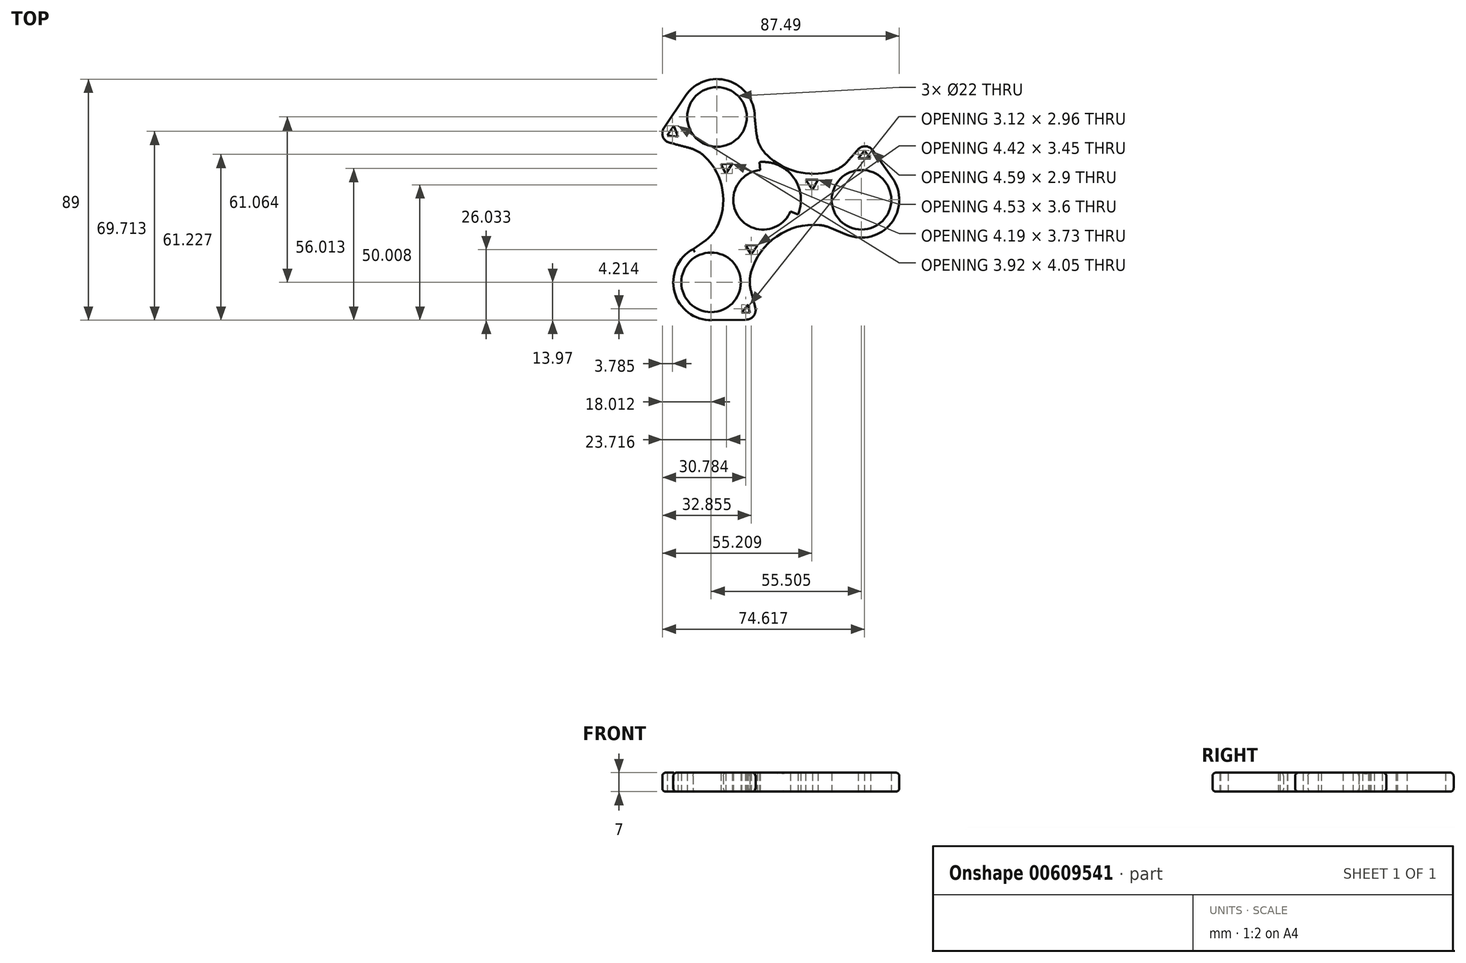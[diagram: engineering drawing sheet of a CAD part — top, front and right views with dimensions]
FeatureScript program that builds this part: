
annotation { "Feature Type Name" : "Feature", "Feature Type Description" : "" }
export const myFeature = defineFeature(function(context is Context, id is Id, definition is map)
    precondition{}
    {
        {
            var Q0;
            Q0=qCreatedBy(makeId("Top.planeOp"),FACE);
            var sketch = newSketch(context, id + "F0", { "sketchPlane" : qUnion([Q0])});
            skLineSegment(sketch, "E0.0", {"start": v(-17.02, 30.58) * mm, "end": v(17.02, 30.58) * mm});
            skLineSegment(sketch, "E0.4", {"start": v(-19.19, -30.48) * mm, "end": v(-35.75, 0) * mm});
            skLineSegment(sketch, "E0.5", {"start": v(-35.75, 0) * mm, "end": v(-17.02, 30.58) * mm});
            skPoint(sketch, "E0.0.midPoint", {"position": v(0, 30.58) * mm});
            skCircle(sketch, "E1", {"center": v(-19.19, -30.48) * mm, "radius": 13.97 * mm});
            skCircle(sketch, "E2", {"center": v(36.32, 0) * mm, "radius": 13.97 * mm});
            skCircle(sketch, "E3", {"center": v(-17.02, 30.58) * mm, "radius": 13.97 * mm});
            skLineSegment(sketch, "E4", {"start": v(-25.86, -18.2) * mm, "end": v(0, 0) * mm});
            skLineSegment(sketch, "E5", {"start": v(0, 0) * mm, "end": v(33.25, -13.86) * mm});
            skLineSegment(sketch, "E6", {"start": v(-3.05, 30.58) * mm, "end": v(0, 0) * mm});
            skPoint(sketch, "E7.0.internal.snap0", {"position": v(0, -30.48) * mm});
            skPoint(sketch, "E8.2.internal.snap0", {"position": v(-9.15, 6.18) * mm});
            skPoint(sketch, "E9.2.internal.snap0", {"position": v(1.12, 10.36) * mm});
            skPoint(sketch, "E10.0.midPoint", {"position": v(0, 45.22) * mm});
            skFitSpline(sketch, "E11", {"points": [v(-5.22, -30.86) * mm, v(-1.7, -44.15) * mm], "startDerivative": vector(4.04, -14.04) * mm, "endDerivative": vector(4.04, -14.04) * mm});
            skFitSpline(sketch, "E12", {"points": [v(38.06, 21.73) * mm, v(28.86, 11.82) * mm], "startDerivative": vector(-10.65, -10) * mm, "endDerivative": vector(-10.65, -10) * mm});
            skFitSpline(sketch, "E13", {"points": [v(-39.36, 22.35) * mm, v(-24.69, 18.5) * mm], "startDerivative": vector(14.18, -3.53) * mm, "endDerivative": vector(14.18, -3.53) * mm});
            skLineSegment(sketch, "E14", {"start": v(-28.63, 38.36) * mm, "end": v(-39.36, 22.35) * mm});
            skLineSegment(sketch, "E15", {"start": v(38.06, 21.73) * mm, "end": v(47.72, 8.07) * mm});
            skLineSegment(sketch, "E16", {"start": v(-18.95, -44.45) * mm, "end": v(-1.7, -44.15) * mm});
            skCircle(sketch, "E17", {"center": v(-17.02, 30.58) * mm, "radius": 11 * mm});
            skCircle(sketch, "E18", {"center": v(36.32, 0) * mm, "radius": 11 * mm});
            skCircle(sketch, "E19", {"center": v(-19.19, -30.48) * mm, "radius": 11 * mm});
            skCircle(sketch, "E20", {"center": v(0, 0) * mm, "radius": 13.97 * mm});
            skCircle(sketch, "E21", {"center": v(0, 0) * mm, "radius": 11 * mm});
            skArc(sketch, "E22", {"start": v(23.12, -9.63) * mm, "mid": v(4.3, -14.03) * mm, "end": v(-5.22, -30.86) * mm});
            skArc(sketch, "E23", {"start": v(-2.06, 20.65) * mm, "mid": v(11.78, 10.56) * mm, "end": v(28.86, 11.82) * mm});
            skArc(sketch, "E24", {"start": v(-19.19, -13.5) * mm, "mid": v(-15, 3.68) * mm, "end": v(-24.69, 18.5) * mm});
            skLineSegment(sketch, "E25", {"start": v(23.12, -9.63) * mm, "end": v(33.25, -13.86) * mm});
            skLineSegment(sketch, "E26", {"start": v(10.45, -4.35) * mm, "end": v(33.25, -13.86) * mm});
            skLineSegment(sketch, "E27", {"start": v(-35.37, 23.76) * mm, "end": v(-33, 27.29) * mm});
            skLineSegment(sketch, "E28", {"start": v(-33, 27.29) * mm, "end": v(-31.46, 23.24) * mm});
            skLineSegment(sketch, "E29", {"start": v(-31.46, 23.24) * mm, "end": v(-35.37, 23.76) * mm});
            skPoint(sketch, "E30.endSnap0", {"position": v(42.9, 14.9) * mm});
            skLineSegment(sketch, "E31", {"start": v(-15.58, 13.08) * mm, "end": v(-13.74, 9.7) * mm});
            skLineSegment(sketch, "E32", {"start": v(-13.74, 9.7) * mm, "end": v(-11.4, 13.43) * mm});
            skLineSegment(sketch, "E33", {"start": v(-11.4, 13.43) * mm, "end": v(-15.58, 13.08) * mm});
            skLineSegment(sketch, "E34", {"start": v(-4.34, -20.14) * mm, "end": v(-2.13, -16.83) * mm});
            skLineSegment(sketch, "E35", {"start": v(-2.13, -16.83) * mm, "end": v(-6.56, -16.69) * mm});
            skLineSegment(sketch, "E36", {"start": v(-6.56, -16.69) * mm, "end": v(-4.34, -20.14) * mm});
            skLineSegment(sketch, "E37", {"start": v(15.74, 7.36) * mm, "end": v(20.27, 7.36) * mm});
            skLineSegment(sketch, "E38", {"start": v(20.27, 7.36) * mm, "end": v(18.17, 3.76) * mm});
            skLineSegment(sketch, "E39", {"start": v(18.17, 3.76) * mm, "end": v(15.74, 7.36) * mm});
            skLineSegment(sketch, "E40", {"start": v(35.12, 15.33) * mm, "end": v(39.71, 15.33) * mm});
            skLineSegment(sketch, "E41", {"start": v(39.71, 15.33) * mm, "end": v(37.39, 18.23) * mm});
            skLineSegment(sketch, "E42", {"start": v(37.39, 18.23) * mm, "end": v(35.12, 15.33) * mm});
            skLineSegment(sketch, "E43", {"start": v(-7.98, -41.63) * mm, "end": v(-5.51, -38.76) * mm});
            skLineSegment(sketch, "E44", {"start": v(-5.51, -38.76) * mm, "end": v(-4.85, -41.71) * mm});
            skLineSegment(sketch, "E45", {"start": v(-4.85, -41.71) * mm, "end": v(-7.98, -41.63) * mm});
            skSolve(sketch);
        }
        {
            var Q0;
            {var subQ0=sQuery(id+"F0.wireOp",EDGE,"E3");var subQ2=sQuery(id+"F0.wireOp",EDGE,"E0.5");var subQ3=makeQuery(id+"F0.imprint","INTERSECT",VERTEX,{"derivedFrom":[subQ2,subQ0]});Q0=makeQuery(id+"F0.imprint","IMPRINT",FACE,{"disambiguationData":[TD([[makeQuery(id+"F0.imprint","IMPRINT",EDGE,{"disambiguationData":[TD([[subQ3,-1.0]])],"derivedFrom":subQ2}),1.0]])]});}
            var Q1;
            {var subQ0=sQuery(id+"F0.wireOp",EDGE,"E13");Q1=makeQuery(id+"F0.imprint","IMPRINT",FACE,{"disambiguationData":[TD([[makeQuery(id+"F0.imprint","IMPRINT",EDGE,{"derivedFrom":subQ0}),1.0]])]});}
            var Q2;
            {var subQ0=sQuery(id+"F0.wireOp",EDGE,"E3");var subQ5=sQuery(id+"F0.wireOp",EDGE,"E0.5");var subQ6=makeQuery(id+"F0.imprint","INTERSECT",VERTEX,{"derivedFrom":[subQ5,subQ0]});Q2=makeQuery(id+"F0.imprint","IMPRINT",FACE,{"disambiguationData":[TD([[makeQuery(id+"F0.imprint","IMPRINT",EDGE,{"disambiguationData":[TD([[subQ6,-1.0]])],"derivedFrom":subQ5}),-1.0]])]});}
            var Q3;
            Q3=makeQuery(id+"F0.imprint","IMPRINT",FACE,{"disambiguationData":[TD([[makeQuery(id+"F0.imprint","IMPRINT",EDGE,{"derivedFrom":sQuery(id+"F0.wireOp",EDGE,"E31")}),-1.0]])]});
            var Q4;
            {var subQ0=sQuery(id+"F0.wireOp",EDGE,"E20");var subQ1=sQuery(id+"F0.wireOp",EDGE,"E4");var subQ2=makeQuery(id+"F0.imprint","INTERSECT",VERTEX,{"derivedFrom":[subQ1,subQ0]});Q4=makeQuery(id+"F0.imprint","IMPRINT",FACE,{"disambiguationData":[TD([[makeQuery(id+"F0.imprint","IMPRINT",EDGE,{"disambiguationData":[TD([[subQ2,-1.0]])],"derivedFrom":subQ1}),1.0]])]});}
            var Q5;
            {var subQ1=sQuery(id+"F0.wireOp",EDGE,"E5");var subQ7=sQuery(id+"F0.wireOp",EDGE,"E26");var subQ9=makeQuery(id+"F0.imprint","INTERSECT",VERTEX,{"derivedFrom":[subQ1,subQ7]});Q5=makeQuery(id+"F0.imprint","IMPRINT",FACE,{"disambiguationData":[TD([[makeQuery(id+"F0.imprint","IMPRINT",EDGE,{"disambiguationData":[TD([[subQ9,1.0]])],"derivedFrom":subQ1}),1.0]])]});}
            var Q6;
            {var subQ0=sQuery(id+"F0.wireOp",EDGE,"E23");Q6=makeQuery(id+"F0.imprint","IMPRINT",FACE,{"disambiguationData":[TD([[makeQuery(id+"F0.imprint","IMPRINT",EDGE,{"derivedFrom":subQ0}),-1.0]])]});}
            var Q7;
            Q7=makeQuery(id+"F0.imprint","IMPRINT",FACE,{"disambiguationData":[TD([[makeQuery(id+"F0.imprint","IMPRINT",EDGE,{"derivedFrom":sQuery(id+"F0.wireOp",EDGE,"E18")}),-1.0]])]});
            var Q8;
            {var subQ8=sQuery(id+"F0.wireOp",EDGE,"E22");Q8=makeQuery(id+"F0.imprint","IMPRINT",FACE,{"disambiguationData":[TD([[makeQuery(id+"F0.imprint","IMPRINT",EDGE,{"derivedFrom":subQ8}),-1.0]])]});}
            var Q9;
            {var subQ1=sQuery(id+"F0.wireOp",EDGE,"E4");var subQ7=sQuery(id+"F0.wireOp",EDGE,"E20");var subQ8=makeQuery(id+"F0.imprint","INTERSECT",VERTEX,{"derivedFrom":[subQ1,subQ7]});Q9=makeQuery(id+"F0.imprint","IMPRINT",FACE,{"disambiguationData":[TD([[makeQuery(id+"F0.imprint","IMPRINT",EDGE,{"disambiguationData":[TD([[subQ8,-1.0]])],"derivedFrom":subQ1}),-1.0]])]});}
            var Q10;
            {var subQ1=sQuery(id+"F0.wireOp",EDGE,"E0.3");var subQ3=sQuery(id+"F0.wireOp",EDGE,"E19");var subQ4=makeQuery(id+"F0.imprint","INTERSECT",VERTEX,{"derivedFrom":[subQ1,subQ3]});Q10=makeQuery(id+"F0.imprint","IMPRINT",FACE,{"disambiguationData":[TD([[makeQuery(id+"F0.imprint","IMPRINT",EDGE,{"disambiguationData":[TD([[subQ4,-1.0]])],"derivedFrom":subQ3}),-1.0]])]});}
            var Q11;
            {var subQ1=sQuery(id+"F0.wireOp",EDGE,"E11");Q11=makeQuery(id+"F0.imprint","IMPRINT",FACE,{"disambiguationData":[TD([[makeQuery(id+"F0.imprint","IMPRINT",EDGE,{"derivedFrom":subQ1}),-1.0]])]});}
            var Q12;
            {var subQ3=sQuery(id+"F0.wireOp",EDGE,"E12");Q12=makeQuery(id+"F0.imprint","IMPRINT",FACE,{"disambiguationData":[TD([[makeQuery(id+"F0.imprint","IMPRINT",EDGE,{"derivedFrom":subQ3}),1.0]])]});}
            var Q13;
            {var subQ1=sQuery(id+"F0.wireOp",EDGE,"E0.3");var subQ4=sQuery(id+"F0.wireOp",EDGE,"E19");var subQ5=makeQuery(id+"F0.imprint","INTERSECT",VERTEX,{"derivedFrom":[subQ1,subQ4]});Q13=makeQuery(id+"F0.imprint","IMPRINT",FACE,{"disambiguationData":[TD([[makeQuery(id+"F0.imprint","IMPRINT",EDGE,{"disambiguationData":[TD([[subQ5,1.0]])],"derivedFrom":subQ4}),-1.0]])]});}
            var Q14;
            Q14=makeQuery(id+"F0.imprint","IMPRINT",FACE,{"disambiguationData":[TD([[makeQuery(id+"F0.imprint","IMPRINT",EDGE,{"derivedFrom":sQuery(id+"F0.wireOp",EDGE,"E19")}),-1.0]])]});
            extrude(context, id + "F1", {"entities" : qUnion([Q0, Q1, Q2, Q3, Q4, Q5, Q6, Q7, Q8, Q9, Q10, Q11, Q12, Q13, Q14]), "depth" : 7 * mm, "offsetDistance" : 25.4 * mm});
        }
        {
            var Q0;
            Q0=makeQuery(id+"F1.opExtrude","SWEPT_EDGE",EDGE,{"disambiguationData":[OSD([sQuery(id+"F0.wireOp",EDGE,"E13"),sQuery(id+"F0.wireOp",EDGE,"E24")])]});
            fillet(context, id + "F2", {"entities" : qUnion([Q0]), "radius" : 12.7 * mm, "tangentPropagation" : true, "rho" : 0.5, "crossSection" : FilletCrossSection.CONIC, "allowEdgeOverflow" : false});
        }
        {
            var Q0;
            Q0=makeQuery(id+"F1.opExtrude","SWEPT_EDGE",EDGE,{"disambiguationData":[OSD([sQuery(id+"F0.wireOp",EDGE,"E0.3"),sQuery(id+"F0.wireOp",EDGE,"E1"),sQuery(id+"F0.wireOp",EDGE,"E11"),sQuery(id+"F0.wireOp",EDGE,"E22")])]});
            var Q1;
            Q1=makeQuery(id+"F1.opExtrude","SWEPT_EDGE",EDGE,{"disambiguationData":[OSD([sQuery(id+"F0.wireOp",EDGE,"E0.1"),sQuery(id+"F0.wireOp",EDGE,"E2"),sQuery(id+"F0.wireOp",EDGE,"E12"),sQuery(id+"F0.wireOp",EDGE,"E23")])]});
            fillet(context, id + "F3", {"entities" : qUnion([Q0, Q1]), "radius" : 12.7 * mm, "tangentPropagation" : true, "rho" : 0.5, "crossSection" : FilletCrossSection.CONIC, "allowEdgeOverflow" : false});
        }
        {
            var Q0;
            Q0=makeQuery(id+"F1.opExtrude","SWEPT_EDGE",EDGE,{"disambiguationData":[OSD([sQuery(id+"F0.wireOp",EDGE,"E6"),sQuery(id+"F0.wireOp",EDGE,"E23")])]});
            var Q1;
            Q1=makeQuery(id+"F1.opExtrude","SWEPT_EDGE",EDGE,{"disambiguationData":[OSD([sQuery(id+"F0.wireOp",EDGE,"E4"),sQuery(id+"F0.wireOp",EDGE,"E24")])]});
            var Q2;
            Q2=makeQuery(id+"F1.opExtrude","SWEPT_EDGE",EDGE,{"disambiguationData":[OSD([sQuery(id+"F0.wireOp",EDGE,"E22"),sQuery(id+"F0.wireOp",EDGE,"E26")])]});
            fillet(context, id + "F4", {"entities" : qUnion([Q0, Q1, Q2]), "radius" : 12.7 * mm, "tangentPropagation" : true, "allowEdgeOverflow" : false});
        }
        {
            var Q0;
            Q0=makeQuery(id+"F1.opExtrude","CAP_EDGE",EDGE,{"disambiguationData":[OSD([sQuery(id+"F0.wireOp",EDGE,"E24")])],"isStart":false});
            var Q1;
            {var subQ0=sQuery(id+"F0.wireOp",EDGE,"E24");var subQ1=sQuery(id+"F0.wireOp",EDGE,"E13");Q1=makeQuery(id+"F2.opFillet","BLEND_EDGE",EDGE,{"blendedFrom":[makeQuery(id+"F1.opExtrude","SWEPT_EDGE",EDGE,{"disambiguationData":[OSD([subQ1,subQ0])]}),makeQuery(id+"F1.opExtrude","CAP_FACE",FACE,{"disambiguationData":[OSD([sQuery(id+"F0.wireOp",EDGE,"E1"),sQuery(id+"F0.wireOp",EDGE,"E2"),sQuery(id+"F0.wireOp",EDGE,"E3"),sQuery(id+"F0.wireOp",EDGE,"E4"),sQuery(id+"F0.wireOp",EDGE,"E6"),sQuery(id+"F0.wireOp",EDGE,"E11"),sQuery(id+"F0.wireOp",EDGE,"E12"),subQ1,sQuery(id+"F0.wireOp",EDGE,"E14"),sQuery(id+"F0.wireOp",EDGE,"E15"),sQuery(id+"F0.wireOp",EDGE,"E16"),sQuery(id+"F0.wireOp",EDGE,"E17"),sQuery(id+"F0.wireOp",EDGE,"E18"),sQuery(id+"F0.wireOp",EDGE,"E19"),sQuery(id+"F0.wireOp",EDGE,"E21"),sQuery(id+"F0.wireOp",EDGE,"E22"),sQuery(id+"F0.wireOp",EDGE,"E23"),subQ0,sQuery(id+"F0.wireOp",EDGE,"E26"),sQuery(id+"F0.wireOp",EDGE,"E27"),sQuery(id+"F0.wireOp",EDGE,"E28"),sQuery(id+"F0.wireOp",EDGE,"E29"),sQuery(id+"F0.wireOp",EDGE,"GTHNUjAg-pZz5-5pDl-8vrh-2y5vtAJtB5Yq"),sQuery(id+"F0.wireOp",EDGE,"E30"),sQuery(id+"F0.wireOp",EDGE,"ZPwYMNyf-sNfp-RKr8-1Stz-misUmBmXIjCw"),sQuery(id+"F0.wireOp",EDGE,"XcAcG1Qn-K1HW-D48b-8TJg-uuhdHlqaHKt2"),sQuery(id+"F0.wireOp",EDGE,"NuKtL48T-xxGD-nBnq-HVJp-iiLt3Cd7KKB5"),sQuery(id+"F0.wireOp",EDGE,"xELJaT0b-NjaD-HxtK-KQ1K-Fbe63v3JBSdq"),sQuery(id+"F0.wireOp",EDGE,"E31"),sQuery(id+"F0.wireOp",EDGE,"E32"),sQuery(id+"F0.wireOp",EDGE,"E33"),sQuery(id+"F0.wireOp",EDGE,"SiT3KE0M-eyeN-RMu0-dXW5-lyOyQHbvpu54"),sQuery(id+"F0.wireOp",EDGE,"M9HWfai5-cRg1-bBkV-RGF1-t70geMIoM3zD"),sQuery(id+"F0.wireOp",EDGE,"RyxoEFKP-Jya3-Pohf-oNvh-z6z1ak4gsZTN"),sQuery(id+"F0.wireOp",EDGE,"E34"),sQuery(id+"F0.wireOp",EDGE,"E35"),sQuery(id+"F0.wireOp",EDGE,"E36")])],"isStart":false})],"blendedInto":[makeQuery(id+"F1.opExtrude","CAP_FACE",FACE,{"disambiguationData":[OSD([sQuery(id+"F0.wireOp",EDGE,"E1"),sQuery(id+"F0.wireOp",EDGE,"E2"),sQuery(id+"F0.wireOp",EDGE,"E3"),sQuery(id+"F0.wireOp",EDGE,"E4"),sQuery(id+"F0.wireOp",EDGE,"E6"),sQuery(id+"F0.wireOp",EDGE,"E11"),sQuery(id+"F0.wireOp",EDGE,"E12"),subQ1,sQuery(id+"F0.wireOp",EDGE,"E14"),sQuery(id+"F0.wireOp",EDGE,"E15"),sQuery(id+"F0.wireOp",EDGE,"E16"),sQuery(id+"F0.wireOp",EDGE,"E17"),sQuery(id+"F0.wireOp",EDGE,"E18"),sQuery(id+"F0.wireOp",EDGE,"E19"),sQuery(id+"F0.wireOp",EDGE,"E21"),sQuery(id+"F0.wireOp",EDGE,"E22"),sQuery(id+"F0.wireOp",EDGE,"E23"),subQ0,sQuery(id+"F0.wireOp",EDGE,"E26"),sQuery(id+"F0.wireOp",EDGE,"E27"),sQuery(id+"F0.wireOp",EDGE,"E28"),sQuery(id+"F0.wireOp",EDGE,"E29"),sQuery(id+"F0.wireOp",EDGE,"GTHNUjAg-pZz5-5pDl-8vrh-2y5vtAJtB5Yq"),sQuery(id+"F0.wireOp",EDGE,"E30"),sQuery(id+"F0.wireOp",EDGE,"ZPwYMNyf-sNfp-RKr8-1Stz-misUmBmXIjCw"),sQuery(id+"F0.wireOp",EDGE,"XcAcG1Qn-K1HW-D48b-8TJg-uuhdHlqaHKt2"),sQuery(id+"F0.wireOp",EDGE,"NuKtL48T-xxGD-nBnq-HVJp-iiLt3Cd7KKB5"),sQuery(id+"F0.wireOp",EDGE,"xELJaT0b-NjaD-HxtK-KQ1K-Fbe63v3JBSdq"),sQuery(id+"F0.wireOp",EDGE,"E31"),sQuery(id+"F0.wireOp",EDGE,"E32"),sQuery(id+"F0.wireOp",EDGE,"E33"),sQuery(id+"F0.wireOp",EDGE,"SiT3KE0M-eyeN-RMu0-dXW5-lyOyQHbvpu54"),sQuery(id+"F0.wireOp",EDGE,"M9HWfai5-cRg1-bBkV-RGF1-t70geMIoM3zD"),sQuery(id+"F0.wireOp",EDGE,"RyxoEFKP-Jya3-Pohf-oNvh-z6z1ak4gsZTN"),sQuery(id+"F0.wireOp",EDGE,"E34"),sQuery(id+"F0.wireOp",EDGE,"E35"),sQuery(id+"F0.wireOp",EDGE,"E36")])],"isStart":false})]});}
            var Q2;
            Q2=makeQuery(id+"F1.opExtrude","CAP_EDGE",EDGE,{"disambiguationData":[OSD([sQuery(id+"F0.wireOp",EDGE,"E13")])],"isStart":false});
            var Q3;
            Q3=makeQuery(id+"F1.opExtrude","CAP_EDGE",EDGE,{"disambiguationData":[OSD([sQuery(id+"F0.wireOp",EDGE,"E14")])],"isStart":false});
            var Q4;
            Q4=makeQuery(id+"F1.opExtrude","CAP_EDGE",EDGE,{"disambiguationData":[OSD([sQuery(id+"F0.wireOp",EDGE,"E3")])],"isStart":false});
            var Q5;
            {var subQ0=sQuery(id+"F0.wireOp",EDGE,"E23");var subQ1=sQuery(id+"F0.wireOp",EDGE,"E12");var subQ2=sQuery(id+"F0.wireOp",EDGE,"E2");Q5=makeQuery(id+"F3.opFillet","BLEND_EDGE",EDGE,{"blendedFrom":[makeQuery(id+"F1.opExtrude","SWEPT_EDGE",EDGE,{"disambiguationData":[OSD([sQuery(id+"F0.wireOp",EDGE,"E0.1"),subQ2,subQ1,subQ0])]}),makeQuery(id+"F1.opExtrude","CAP_FACE",FACE,{"disambiguationData":[OSD([sQuery(id+"F0.wireOp",EDGE,"E1"),subQ2,sQuery(id+"F0.wireOp",EDGE,"E3"),sQuery(id+"F0.wireOp",EDGE,"E4"),sQuery(id+"F0.wireOp",EDGE,"E6"),sQuery(id+"F0.wireOp",EDGE,"E11"),subQ1,sQuery(id+"F0.wireOp",EDGE,"E13"),sQuery(id+"F0.wireOp",EDGE,"E14"),sQuery(id+"F0.wireOp",EDGE,"E15"),sQuery(id+"F0.wireOp",EDGE,"E16"),sQuery(id+"F0.wireOp",EDGE,"E17"),sQuery(id+"F0.wireOp",EDGE,"E18"),sQuery(id+"F0.wireOp",EDGE,"E19"),sQuery(id+"F0.wireOp",EDGE,"E21"),sQuery(id+"F0.wireOp",EDGE,"E22"),subQ0,sQuery(id+"F0.wireOp",EDGE,"E24"),sQuery(id+"F0.wireOp",EDGE,"E26"),sQuery(id+"F0.wireOp",EDGE,"E27"),sQuery(id+"F0.wireOp",EDGE,"E28"),sQuery(id+"F0.wireOp",EDGE,"E29"),sQuery(id+"F0.wireOp",EDGE,"GTHNUjAg-pZz5-5pDl-8vrh-2y5vtAJtB5Yq"),sQuery(id+"F0.wireOp",EDGE,"E30"),sQuery(id+"F0.wireOp",EDGE,"ZPwYMNyf-sNfp-RKr8-1Stz-misUmBmXIjCw"),sQuery(id+"F0.wireOp",EDGE,"XcAcG1Qn-K1HW-D48b-8TJg-uuhdHlqaHKt2"),sQuery(id+"F0.wireOp",EDGE,"NuKtL48T-xxGD-nBnq-HVJp-iiLt3Cd7KKB5"),sQuery(id+"F0.wireOp",EDGE,"xELJaT0b-NjaD-HxtK-KQ1K-Fbe63v3JBSdq"),sQuery(id+"F0.wireOp",EDGE,"E31"),sQuery(id+"F0.wireOp",EDGE,"E32"),sQuery(id+"F0.wireOp",EDGE,"E33"),sQuery(id+"F0.wireOp",EDGE,"SiT3KE0M-eyeN-RMu0-dXW5-lyOyQHbvpu54"),sQuery(id+"F0.wireOp",EDGE,"M9HWfai5-cRg1-bBkV-RGF1-t70geMIoM3zD"),sQuery(id+"F0.wireOp",EDGE,"RyxoEFKP-Jya3-Pohf-oNvh-z6z1ak4gsZTN"),sQuery(id+"F0.wireOp",EDGE,"E34"),sQuery(id+"F0.wireOp",EDGE,"E35"),sQuery(id+"F0.wireOp",EDGE,"E36")])],"isStart":false})],"blendedInto":[makeQuery(id+"F1.opExtrude","CAP_FACE",FACE,{"disambiguationData":[OSD([sQuery(id+"F0.wireOp",EDGE,"E1"),subQ2,sQuery(id+"F0.wireOp",EDGE,"E3"),sQuery(id+"F0.wireOp",EDGE,"E4"),sQuery(id+"F0.wireOp",EDGE,"E6"),sQuery(id+"F0.wireOp",EDGE,"E11"),subQ1,sQuery(id+"F0.wireOp",EDGE,"E13"),sQuery(id+"F0.wireOp",EDGE,"E14"),sQuery(id+"F0.wireOp",EDGE,"E15"),sQuery(id+"F0.wireOp",EDGE,"E16"),sQuery(id+"F0.wireOp",EDGE,"E17"),sQuery(id+"F0.wireOp",EDGE,"E18"),sQuery(id+"F0.wireOp",EDGE,"E19"),sQuery(id+"F0.wireOp",EDGE,"E21"),sQuery(id+"F0.wireOp",EDGE,"E22"),subQ0,sQuery(id+"F0.wireOp",EDGE,"E24"),sQuery(id+"F0.wireOp",EDGE,"E26"),sQuery(id+"F0.wireOp",EDGE,"E27"),sQuery(id+"F0.wireOp",EDGE,"E28"),sQuery(id+"F0.wireOp",EDGE,"E29"),sQuery(id+"F0.wireOp",EDGE,"GTHNUjAg-pZz5-5pDl-8vrh-2y5vtAJtB5Yq"),sQuery(id+"F0.wireOp",EDGE,"E30"),sQuery(id+"F0.wireOp",EDGE,"ZPwYMNyf-sNfp-RKr8-1Stz-misUmBmXIjCw"),sQuery(id+"F0.wireOp",EDGE,"XcAcG1Qn-K1HW-D48b-8TJg-uuhdHlqaHKt2"),sQuery(id+"F0.wireOp",EDGE,"NuKtL48T-xxGD-nBnq-HVJp-iiLt3Cd7KKB5"),sQuery(id+"F0.wireOp",EDGE,"xELJaT0b-NjaD-HxtK-KQ1K-Fbe63v3JBSdq"),sQuery(id+"F0.wireOp",EDGE,"E31"),sQuery(id+"F0.wireOp",EDGE,"E32"),sQuery(id+"F0.wireOp",EDGE,"E33"),sQuery(id+"F0.wireOp",EDGE,"SiT3KE0M-eyeN-RMu0-dXW5-lyOyQHbvpu54"),sQuery(id+"F0.wireOp",EDGE,"M9HWfai5-cRg1-bBkV-RGF1-t70geMIoM3zD"),sQuery(id+"F0.wireOp",EDGE,"RyxoEFKP-Jya3-Pohf-oNvh-z6z1ak4gsZTN"),sQuery(id+"F0.wireOp",EDGE,"E34"),sQuery(id+"F0.wireOp",EDGE,"E35"),sQuery(id+"F0.wireOp",EDGE,"E36")])],"isStart":false})]});}
            var Q6;
            Q6=makeQuery(id+"F1.opExtrude","CAP_EDGE",EDGE,{"disambiguationData":[OSD([sQuery(id+"F0.wireOp",EDGE,"E12")])],"isStart":false});
            var Q7;
            Q7=makeQuery(id+"F1.opExtrude","CAP_EDGE",EDGE,{"disambiguationData":[OSD([sQuery(id+"F0.wireOp",EDGE,"E15")])],"isStart":false});
            var Q8;
            Q8=makeQuery(id+"F1.opExtrude","CAP_EDGE",EDGE,{"disambiguationData":[OSD([sQuery(id+"F0.wireOp",EDGE,"E2")])],"isStart":false});
            var Q9;
            Q9=makeQuery(id+"F1.opExtrude","CAP_EDGE",EDGE,{"disambiguationData":[OSD([sQuery(id+"F0.wireOp",EDGE,"E16")])],"isStart":false});
            var Q10;
            Q10=makeQuery(id+"F1.opExtrude","CAP_EDGE",EDGE,{"disambiguationData":[OSD([sQuery(id+"F0.wireOp",EDGE,"E1")])],"isStart":false});
            var Q11;
            Q11=makeQuery(id+"F1.opExtrude","CAP_EDGE",EDGE,{"disambiguationData":[OSD([sQuery(id+"F0.wireOp",EDGE,"E14")])],"isStart":true});
            var Q12;
            Q12=makeQuery(id+"F1.opExtrude","SWEPT_FACE",FACE,{"disambiguationData":[OSD([sQuery(id+"F0.wireOp",EDGE,"E3")])]});
            var Q13;
            {var subQ0=sQuery(id+"F0.wireOp",EDGE,"E23");var subQ1=sQuery(id+"F0.wireOp",EDGE,"E6");Q13=makeQuery(id+"F4.opFillet","BLEND_EDGE",EDGE,{"blendedFrom":[makeQuery(id+"F1.opExtrude","SWEPT_EDGE",EDGE,{"disambiguationData":[OSD([subQ1,subQ0])]}),makeQuery(id+"F1.opExtrude","CAP_FACE",FACE,{"disambiguationData":[OSD([sQuery(id+"F0.wireOp",EDGE,"E1"),sQuery(id+"F0.wireOp",EDGE,"E2"),sQuery(id+"F0.wireOp",EDGE,"E3"),sQuery(id+"F0.wireOp",EDGE,"E4"),subQ1,sQuery(id+"F0.wireOp",EDGE,"E11"),sQuery(id+"F0.wireOp",EDGE,"E12"),sQuery(id+"F0.wireOp",EDGE,"E13"),sQuery(id+"F0.wireOp",EDGE,"E14"),sQuery(id+"F0.wireOp",EDGE,"E15"),sQuery(id+"F0.wireOp",EDGE,"E16"),sQuery(id+"F0.wireOp",EDGE,"E17"),sQuery(id+"F0.wireOp",EDGE,"E18"),sQuery(id+"F0.wireOp",EDGE,"E19"),sQuery(id+"F0.wireOp",EDGE,"E21"),sQuery(id+"F0.wireOp",EDGE,"E22"),subQ0,sQuery(id+"F0.wireOp",EDGE,"E24"),sQuery(id+"F0.wireOp",EDGE,"E26"),sQuery(id+"F0.wireOp",EDGE,"E27"),sQuery(id+"F0.wireOp",EDGE,"E28"),sQuery(id+"F0.wireOp",EDGE,"E29"),sQuery(id+"F0.wireOp",EDGE,"GTHNUjAg-pZz5-5pDl-8vrh-2y5vtAJtB5Yq"),sQuery(id+"F0.wireOp",EDGE,"E30"),sQuery(id+"F0.wireOp",EDGE,"ZPwYMNyf-sNfp-RKr8-1Stz-misUmBmXIjCw"),sQuery(id+"F0.wireOp",EDGE,"XcAcG1Qn-K1HW-D48b-8TJg-uuhdHlqaHKt2"),sQuery(id+"F0.wireOp",EDGE,"NuKtL48T-xxGD-nBnq-HVJp-iiLt3Cd7KKB5"),sQuery(id+"F0.wireOp",EDGE,"xELJaT0b-NjaD-HxtK-KQ1K-Fbe63v3JBSdq"),sQuery(id+"F0.wireOp",EDGE,"E31"),sQuery(id+"F0.wireOp",EDGE,"E32"),sQuery(id+"F0.wireOp",EDGE,"E33"),sQuery(id+"F0.wireOp",EDGE,"SiT3KE0M-eyeN-RMu0-dXW5-lyOyQHbvpu54"),sQuery(id+"F0.wireOp",EDGE,"M9HWfai5-cRg1-bBkV-RGF1-t70geMIoM3zD"),sQuery(id+"F0.wireOp",EDGE,"RyxoEFKP-Jya3-Pohf-oNvh-z6z1ak4gsZTN"),sQuery(id+"F0.wireOp",EDGE,"E34"),sQuery(id+"F0.wireOp",EDGE,"E35"),sQuery(id+"F0.wireOp",EDGE,"E36")])],"isStart":true})],"blendedInto":[makeQuery(id+"F1.opExtrude","CAP_FACE",FACE,{"disambiguationData":[OSD([sQuery(id+"F0.wireOp",EDGE,"E1"),sQuery(id+"F0.wireOp",EDGE,"E2"),sQuery(id+"F0.wireOp",EDGE,"E3"),sQuery(id+"F0.wireOp",EDGE,"E4"),subQ1,sQuery(id+"F0.wireOp",EDGE,"E11"),sQuery(id+"F0.wireOp",EDGE,"E12"),sQuery(id+"F0.wireOp",EDGE,"E13"),sQuery(id+"F0.wireOp",EDGE,"E14"),sQuery(id+"F0.wireOp",EDGE,"E15"),sQuery(id+"F0.wireOp",EDGE,"E16"),sQuery(id+"F0.wireOp",EDGE,"E17"),sQuery(id+"F0.wireOp",EDGE,"E18"),sQuery(id+"F0.wireOp",EDGE,"E19"),sQuery(id+"F0.wireOp",EDGE,"E21"),sQuery(id+"F0.wireOp",EDGE,"E22"),subQ0,sQuery(id+"F0.wireOp",EDGE,"E24"),sQuery(id+"F0.wireOp",EDGE,"E26"),sQuery(id+"F0.wireOp",EDGE,"E27"),sQuery(id+"F0.wireOp",EDGE,"E28"),sQuery(id+"F0.wireOp",EDGE,"E29"),sQuery(id+"F0.wireOp",EDGE,"GTHNUjAg-pZz5-5pDl-8vrh-2y5vtAJtB5Yq"),sQuery(id+"F0.wireOp",EDGE,"E30"),sQuery(id+"F0.wireOp",EDGE,"ZPwYMNyf-sNfp-RKr8-1Stz-misUmBmXIjCw"),sQuery(id+"F0.wireOp",EDGE,"XcAcG1Qn-K1HW-D48b-8TJg-uuhdHlqaHKt2"),sQuery(id+"F0.wireOp",EDGE,"NuKtL48T-xxGD-nBnq-HVJp-iiLt3Cd7KKB5"),sQuery(id+"F0.wireOp",EDGE,"xELJaT0b-NjaD-HxtK-KQ1K-Fbe63v3JBSdq"),sQuery(id+"F0.wireOp",EDGE,"E31"),sQuery(id+"F0.wireOp",EDGE,"E32"),sQuery(id+"F0.wireOp",EDGE,"E33"),sQuery(id+"F0.wireOp",EDGE,"SiT3KE0M-eyeN-RMu0-dXW5-lyOyQHbvpu54"),sQuery(id+"F0.wireOp",EDGE,"M9HWfai5-cRg1-bBkV-RGF1-t70geMIoM3zD"),sQuery(id+"F0.wireOp",EDGE,"RyxoEFKP-Jya3-Pohf-oNvh-z6z1ak4gsZTN"),sQuery(id+"F0.wireOp",EDGE,"E34"),sQuery(id+"F0.wireOp",EDGE,"E35"),sQuery(id+"F0.wireOp",EDGE,"E36")])],"isStart":true})]});}
            var Q14;
            Q14=makeQuery(id+"F1.opExtrude","CAP_EDGE",EDGE,{"disambiguationData":[OSD([sQuery(id+"F0.wireOp",EDGE,"E2")])],"isStart":true});
            var Q15;
            Q15=makeQuery(id+"F1.opExtrude","CAP_EDGE",EDGE,{"disambiguationData":[OSD([sQuery(id+"F0.wireOp",EDGE,"E15")])],"isStart":true});
            var Q16;
            Q16=makeQuery(id+"F1.opExtrude","CAP_EDGE",EDGE,{"disambiguationData":[OSD([sQuery(id+"F0.wireOp",EDGE,"E16")])],"isStart":true});
            var Q17;
            Q17=makeQuery(id+"F1.opExtrude","CAP_EDGE",EDGE,{"disambiguationData":[OSD([sQuery(id+"F0.wireOp",EDGE,"E1")])],"isStart":true});
            var Q18;
            Q18=makeQuery(id+"F1.opExtrude","CAP_EDGE",EDGE,{"disambiguationData":[OSD([sQuery(id+"F0.wireOp",EDGE,"E24")])],"isStart":true});
            var Q19;
            {var subQ0=sQuery(id+"F0.wireOp",EDGE,"E24");var subQ1=sQuery(id+"F0.wireOp",EDGE,"E4");Q19=makeQuery(id+"F4.opFillet","BLEND_EDGE",EDGE,{"blendedFrom":[makeQuery(id+"F1.opExtrude","SWEPT_EDGE",EDGE,{"disambiguationData":[OSD([subQ1,subQ0])]}),makeQuery(id+"F1.opExtrude","CAP_FACE",FACE,{"disambiguationData":[OSD([sQuery(id+"F0.wireOp",EDGE,"E1"),sQuery(id+"F0.wireOp",EDGE,"E2"),sQuery(id+"F0.wireOp",EDGE,"E3"),subQ1,sQuery(id+"F0.wireOp",EDGE,"E6"),sQuery(id+"F0.wireOp",EDGE,"E11"),sQuery(id+"F0.wireOp",EDGE,"E12"),sQuery(id+"F0.wireOp",EDGE,"E13"),sQuery(id+"F0.wireOp",EDGE,"E14"),sQuery(id+"F0.wireOp",EDGE,"E15"),sQuery(id+"F0.wireOp",EDGE,"E16"),sQuery(id+"F0.wireOp",EDGE,"E17"),sQuery(id+"F0.wireOp",EDGE,"E18"),sQuery(id+"F0.wireOp",EDGE,"E19"),sQuery(id+"F0.wireOp",EDGE,"E21"),sQuery(id+"F0.wireOp",EDGE,"E22"),sQuery(id+"F0.wireOp",EDGE,"E23"),subQ0,sQuery(id+"F0.wireOp",EDGE,"E26"),sQuery(id+"F0.wireOp",EDGE,"E27"),sQuery(id+"F0.wireOp",EDGE,"E28"),sQuery(id+"F0.wireOp",EDGE,"E29"),sQuery(id+"F0.wireOp",EDGE,"GTHNUjAg-pZz5-5pDl-8vrh-2y5vtAJtB5Yq"),sQuery(id+"F0.wireOp",EDGE,"E30"),sQuery(id+"F0.wireOp",EDGE,"ZPwYMNyf-sNfp-RKr8-1Stz-misUmBmXIjCw"),sQuery(id+"F0.wireOp",EDGE,"XcAcG1Qn-K1HW-D48b-8TJg-uuhdHlqaHKt2"),sQuery(id+"F0.wireOp",EDGE,"NuKtL48T-xxGD-nBnq-HVJp-iiLt3Cd7KKB5"),sQuery(id+"F0.wireOp",EDGE,"xELJaT0b-NjaD-HxtK-KQ1K-Fbe63v3JBSdq"),sQuery(id+"F0.wireOp",EDGE,"E31"),sQuery(id+"F0.wireOp",EDGE,"E32"),sQuery(id+"F0.wireOp",EDGE,"E33"),sQuery(id+"F0.wireOp",EDGE,"SiT3KE0M-eyeN-RMu0-dXW5-lyOyQHbvpu54"),sQuery(id+"F0.wireOp",EDGE,"M9HWfai5-cRg1-bBkV-RGF1-t70geMIoM3zD"),sQuery(id+"F0.wireOp",EDGE,"RyxoEFKP-Jya3-Pohf-oNvh-z6z1ak4gsZTN"),sQuery(id+"F0.wireOp",EDGE,"E34"),sQuery(id+"F0.wireOp",EDGE,"E35"),sQuery(id+"F0.wireOp",EDGE,"E36")])],"isStart":true})],"blendedInto":[makeQuery(id+"F1.opExtrude","CAP_FACE",FACE,{"disambiguationData":[OSD([sQuery(id+"F0.wireOp",EDGE,"E1"),sQuery(id+"F0.wireOp",EDGE,"E2"),sQuery(id+"F0.wireOp",EDGE,"E3"),subQ1,sQuery(id+"F0.wireOp",EDGE,"E6"),sQuery(id+"F0.wireOp",EDGE,"E11"),sQuery(id+"F0.wireOp",EDGE,"E12"),sQuery(id+"F0.wireOp",EDGE,"E13"),sQuery(id+"F0.wireOp",EDGE,"E14"),sQuery(id+"F0.wireOp",EDGE,"E15"),sQuery(id+"F0.wireOp",EDGE,"E16"),sQuery(id+"F0.wireOp",EDGE,"E17"),sQuery(id+"F0.wireOp",EDGE,"E18"),sQuery(id+"F0.wireOp",EDGE,"E19"),sQuery(id+"F0.wireOp",EDGE,"E21"),sQuery(id+"F0.wireOp",EDGE,"E22"),sQuery(id+"F0.wireOp",EDGE,"E23"),subQ0,sQuery(id+"F0.wireOp",EDGE,"E26"),sQuery(id+"F0.wireOp",EDGE,"E27"),sQuery(id+"F0.wireOp",EDGE,"E28"),sQuery(id+"F0.wireOp",EDGE,"E29"),sQuery(id+"F0.wireOp",EDGE,"GTHNUjAg-pZz5-5pDl-8vrh-2y5vtAJtB5Yq"),sQuery(id+"F0.wireOp",EDGE,"E30"),sQuery(id+"F0.wireOp",EDGE,"ZPwYMNyf-sNfp-RKr8-1Stz-misUmBmXIjCw"),sQuery(id+"F0.wireOp",EDGE,"XcAcG1Qn-K1HW-D48b-8TJg-uuhdHlqaHKt2"),sQuery(id+"F0.wireOp",EDGE,"NuKtL48T-xxGD-nBnq-HVJp-iiLt3Cd7KKB5"),sQuery(id+"F0.wireOp",EDGE,"xELJaT0b-NjaD-HxtK-KQ1K-Fbe63v3JBSdq"),sQuery(id+"F0.wireOp",EDGE,"E31"),sQuery(id+"F0.wireOp",EDGE,"E32"),sQuery(id+"F0.wireOp",EDGE,"E33"),sQuery(id+"F0.wireOp",EDGE,"SiT3KE0M-eyeN-RMu0-dXW5-lyOyQHbvpu54"),sQuery(id+"F0.wireOp",EDGE,"M9HWfai5-cRg1-bBkV-RGF1-t70geMIoM3zD"),sQuery(id+"F0.wireOp",EDGE,"RyxoEFKP-Jya3-Pohf-oNvh-z6z1ak4gsZTN"),sQuery(id+"F0.wireOp",EDGE,"E34"),sQuery(id+"F0.wireOp",EDGE,"E35"),sQuery(id+"F0.wireOp",EDGE,"E36")])],"isStart":true})]});}
            fillet(context, id + "F5", {"entities" : qUnion([Q0, Q1, Q2, Q3, Q4, Q5, Q6, Q7, Q8, Q9, Q10, Q11, Q12, Q13, Q14, Q15, Q16, Q17, Q18, Q19]), "radius" : 1.27 * mm, "tangentPropagation" : true, "allowEdgeOverflow" : false});
        }
        {
            var Q0;
            Q0=makeQuery(id+"F1.opExtrude","SWEPT_EDGE",EDGE,{"disambiguationData":[OSD([sQuery(id+"F0.wireOp",EDGE,"E11"),sQuery(id+"F0.wireOp",EDGE,"E16")])]});
            var Q1;
            Q1=makeQuery(id+"F1.opExtrude","SWEPT_EDGE",EDGE,{"disambiguationData":[OSD([sQuery(id+"F0.wireOp",EDGE,"E12"),sQuery(id+"F0.wireOp",EDGE,"E15")])]});
            var Q2;
            Q2=makeQuery(id+"F1.opExtrude","SWEPT_EDGE",EDGE,{"disambiguationData":[OSD([sQuery(id+"F0.wireOp",EDGE,"E13"),sQuery(id+"F0.wireOp",EDGE,"E14")])]});
            fillet(context, id + "F6", {"entities" : qUnion([Q0, Q1, Q2]), "radius" : 3.5 * mm, "tangentPropagation" : true, "allowEdgeOverflow" : false});
        }
    });
